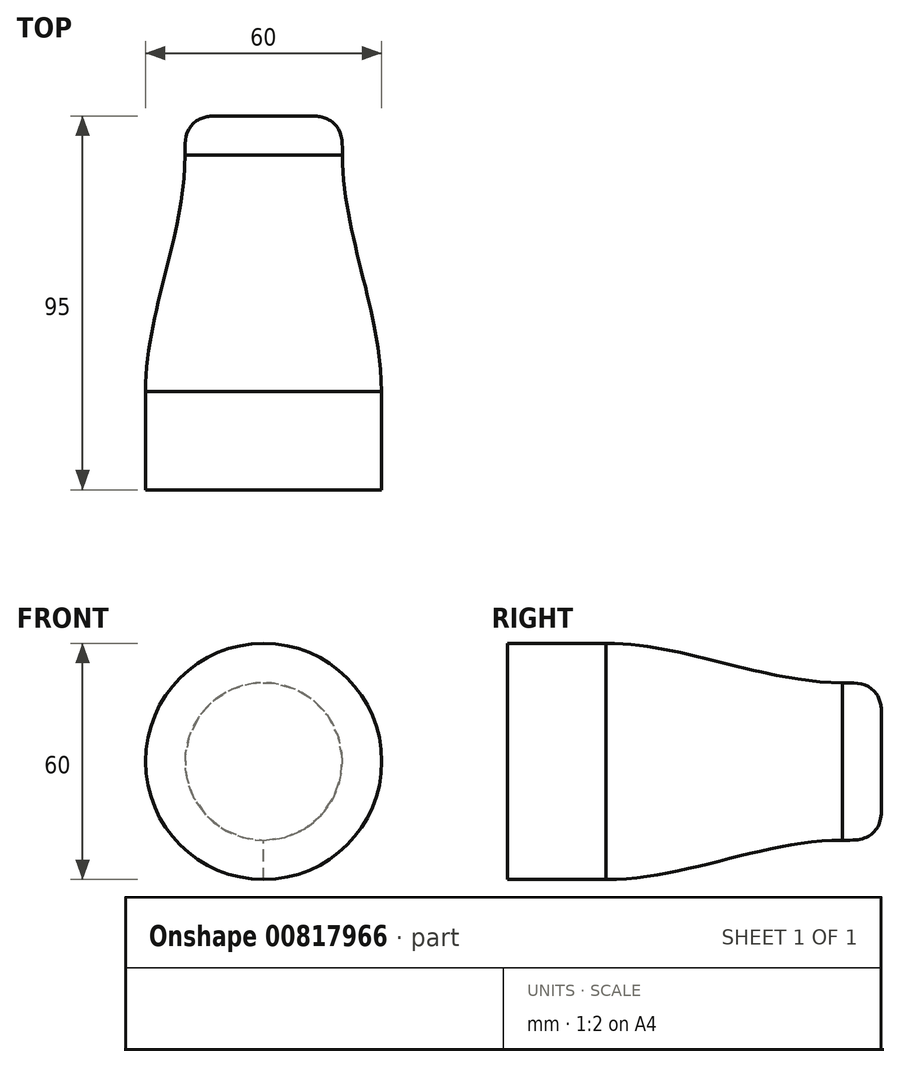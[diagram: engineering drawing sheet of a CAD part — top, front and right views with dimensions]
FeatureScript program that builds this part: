
annotation { "Feature Type Name" : "Feature", "Feature Type Description" : "" }
export const myFeature = defineFeature(function(context is Context, id is Id, definition is map)
    precondition{}
    {
        {
            var Q0;
            Q0=qCreatedBy(makeId("Front.planeOp"),FACE);
            var sketch = newSketch(context, id + "F0", { "sketchPlane" : qUnion([Q0])});
            skCircle(sketch, "E0", {"center": v(0, 0) * mm, "radius": 30 * mm});
            skSolve(sketch);
        }
        {
            var Q0;
            Q0=qCreatedBy(makeId("Front.planeOp"),FACE);
            cPlane(context, id + "F1", {"entities" : qUnion([Q0]), "cplaneType" : CPlaneType.OFFSET, "offset" : 25 * mm, "oppositeDirection" : true, "width" : 150 * mm, "height" : 150 * mm});
        }
        {
            var Q0;
            Q0=makeQuery(id+"F0.imprint","IMPRINT",FACE,{"disambiguationData":[TD([[makeQuery(id+"F0.imprint","IMPRINT",EDGE,{"derivedFrom":sQuery(id+"F0.wireOp",EDGE,"E0")}),1.0]])]});
            extrude(context, id + "F2", {"entities" : qUnion([Q0]), "oppositeDirection" : true, "depth" : 25 * mm, "offsetDistance" : 25 * mm});
        }
        {
            var Q0;
            Q0=makeQuery(id+"F2.opExtrude","CAP_FACE",FACE,{"disambiguationData":[OSD([sQuery(id+"F0.wireOp",EDGE,"E0")])],"isStart":false});
            var sketch = newSketch(context, id + "F3", { "sketchPlane" : qUnion([Q0])});
            skCircle(sketch, "E1", {"center": v(0, 0) * mm, "radius": 30 * mm});
            skSolve(sketch);
        }
        {
            var Q0;
            Q0=qCreatedBy(id+"F1.planeOp",FACE);
            cPlane(context, id + "F4", {"entities" : qUnion([Q0]), "cplaneType" : CPlaneType.OFFSET, "offset" : 60 * mm, "oppositeDirection" : true, "width" : 150 * mm, "height" : 150 * mm});
        }
        {
            var Q0;
            Q0=qCreatedBy(id+"F4.planeOp",FACE);
            var sketch = newSketch(context, id + "F5", { "sketchPlane" : qUnion([Q0])});
            skCircle(sketch, "E2", {"center": v(0, 0) * mm, "radius": 20 * mm});
            skSolve(sketch);
        }
        {
            var Q0;
            Q0=makeQuery(id+"F3.imprint","IMPRINT",FACE,{"disambiguationData":[TD([[makeQuery(id+"F3.imprint","IMPRINT",EDGE,{"derivedFrom":sQuery(id+"F3.wireOp",EDGE,"E1")}),-1.0]])]});
            var Q1;
            Q1 = qSketchRegion(id + "F5", true);
            loft(context, id + "F6", {"startCondition" : LoftEndDerivativeType.NORMAL_TO_PROFILE, "startMagnitude" : 1, "endCondition" : LoftEndDerivativeType.NORMAL_TO_PROFILE, "endMagnitude" : 1, "sheetProfilesArray" : [{ "sheetProfileEntities" : qUnion([Q0]) }, { "sheetProfileEntities" : qUnion([Q1]) }]});
        }
        {
            var Q0;
            Q0=makeQuery(id+"F5.imprint","IMPRINT",FACE,{"disambiguationData":[TD([[makeQuery(id+"F5.imprint","IMPRINT",EDGE,{"derivedFrom":sQuery(id+"F5.wireOp",EDGE,"E2")}),1.0]])]});
            var sketch = newSketch(context, id + "F7", { "sketchPlane" : qUnion([Q0])});
            skCircle(sketch, "E3", {"center": v(0, 0) * mm, "radius": 20 * mm});
            skSolve(sketch);
        }
        {
            var Q0;
            Q0 = qSketchRegion(id + "F7", true);
            extrude(context, id + "F8", {"entities" : qUnion([Q0]), "oppositeDirection" : true, "depth" : 10 * mm, "offsetDistance" : 25 * mm});
        }
        {
            var Q0;
            Q0=makeQuery(id+"F8.opExtrude","CAP_EDGE",EDGE,{"disambiguationData":[OSD([sQuery(id+"F7.wireOp",EDGE,"E3")])],"isStart":false});
            fillet(context, id + "F9", {"entities" : qUnion([Q0]), "radius" : 8 * mm, "tangentPropagation" : true, "rho" : 0.5, "crossSection" : FilletCrossSection.CONIC, "allowEdgeOverflow" : false});
        }
    });
